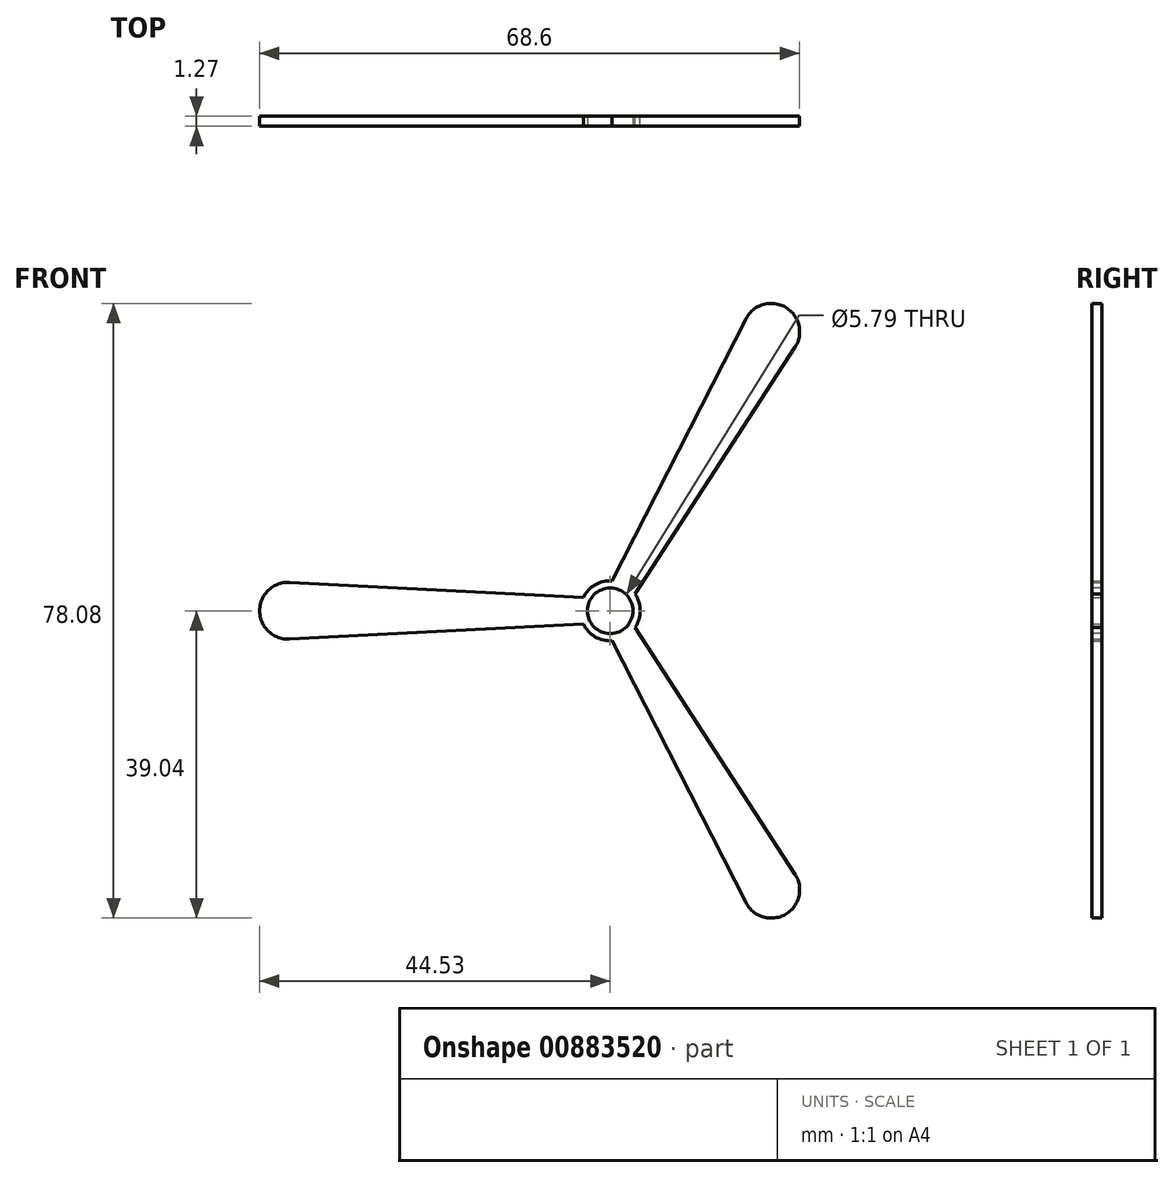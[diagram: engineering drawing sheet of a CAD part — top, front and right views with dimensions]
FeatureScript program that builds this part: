
annotation { "Feature Type Name" : "Feature", "Feature Type Description" : "" }
export const myFeature = defineFeature(function(context is Context, id is Id, definition is map)
    precondition{}
    {
        {
            var Q0;
            Q0=qCreatedBy(makeId("Front.planeOp"),FACE);
            var sketch = newSketch(context, id + "F0", { "sketchPlane" : qUnion([Q0])});
            skArc(sketch, "E0", {"start": v(3.81, 0) * mm, "mid": v(3.65, 1.1) * mm, "end": v(3.17, 2.12) * mm});
            skLineSegment(sketch, "E1", {"start": v(-3.42, 1.69) * mm, "end": v(-40.73, 3.6) * mm});
            skLineSegment(sketch, "E2.MirrorCS", {"start": v(-3.42, -1.69) * mm, "end": v(-40.73, -3.6) * mm});
            skArc(sketch, "E3.MirrorCS", {"start": v(3.81, 0) * mm, "mid": v(3.65, -1.1) * mm, "end": v(3.17, -2.12) * mm});
            skArc(sketch, "E4", {"start": v(-40.73, 3.6) * mm, "mid": v(-44.53, 0) * mm, "end": v(-40.73, -3.6) * mm});
            skLineSegment(sketch, "E5.1.0", {"start": v(0.25, -3.8) * mm, "end": v(17.25, -37.08) * mm});
            skLineSegment(sketch, "E5.1.1", {"start": v(3.17, -2.12) * mm, "end": v(23.49, -33.48) * mm});
            skArc(sketch, "E5.1.2", {"start": v(17.25, -37.08) * mm, "mid": v(22.26, -38.56) * mm, "end": v(23.49, -33.48) * mm});
            skLineSegment(sketch, "E5.2.0", {"start": v(3.17, 2.12) * mm, "end": v(23.49, 33.48) * mm});
            skLineSegment(sketch, "E5.2.1", {"start": v(0.25, 3.8) * mm, "end": v(17.25, 37.08) * mm});
            skArc(sketch, "E5.2.2", {"start": v(23.49, 33.48) * mm, "mid": v(22.26, 38.56) * mm, "end": v(17.25, 37.08) * mm});
            skArc(sketch, "E6.trimOffspring", {"start": v(0.25, 3.8) * mm, "mid": v(-1.9, 3.3) * mm, "end": v(-3.42, 1.69) * mm});
            skArc(sketch, "E7.trimOffspring", {"start": v(0.25, -3.8) * mm, "mid": v(-1.9, -3.3) * mm, "end": v(-3.42, -1.69) * mm});
            skSolve(sketch);
        }
        {
            var Q0;
            Q0 = qSketchRegion(id + "F0", true);
            extrude(context, id + "F1", {"entities" : qUnion([Q0]), "depth" : 1.27 * mm, "offsetDistance" : 25.4 * mm});
        }
        {
            var Q0;
            Q0=makeQuery(id+"F1.opExtrude","CAP_FACE",FACE,{"disambiguationData":[OSD([sQuery(id+"F0.wireOp",EDGE,"E0"),sQuery(id+"F0.wireOp",EDGE,"E1"),sQuery(id+"F0.wireOp",EDGE,"E2.MirrorCS"),sQuery(id+"F0.wireOp",EDGE,"E3.MirrorCS"),sQuery(id+"F0.wireOp",EDGE,"E4"),sQuery(id+"F0.wireOp",EDGE,"E5.1.0"),sQuery(id+"F0.wireOp",EDGE,"E5.1.1"),sQuery(id+"F0.wireOp",EDGE,"E5.1.2"),sQuery(id+"F0.wireOp",EDGE,"E5.2.0"),sQuery(id+"F0.wireOp",EDGE,"E5.2.1"),sQuery(id+"F0.wireOp",EDGE,"E5.2.2"),sQuery(id+"F0.wireOp",EDGE,"E6.trimOffspring"),sQuery(id+"F0.wireOp",EDGE,"E7.trimOffspring")])],"isStart":false});
            var sketch = newSketch(context, id + "F2", { "sketchPlane" : qUnion([Q0])});
            skCircle(sketch, "E8", {"center": v(0, 0) * mm, "radius": 2.9 * mm});
            skSolve(sketch);
        }
        {
            var Q0;
            Q0 = qSketchRegion(id + "F2", true);
            extrude(context, id + "F3", {"entities" : qUnion([Q0]), "operationType" : NewBodyOperationType.REMOVE, "oppositeDirection" : true, "depth" : 25.4 * mm, "offsetDistance" : 25.4 * mm});
        }
    });
